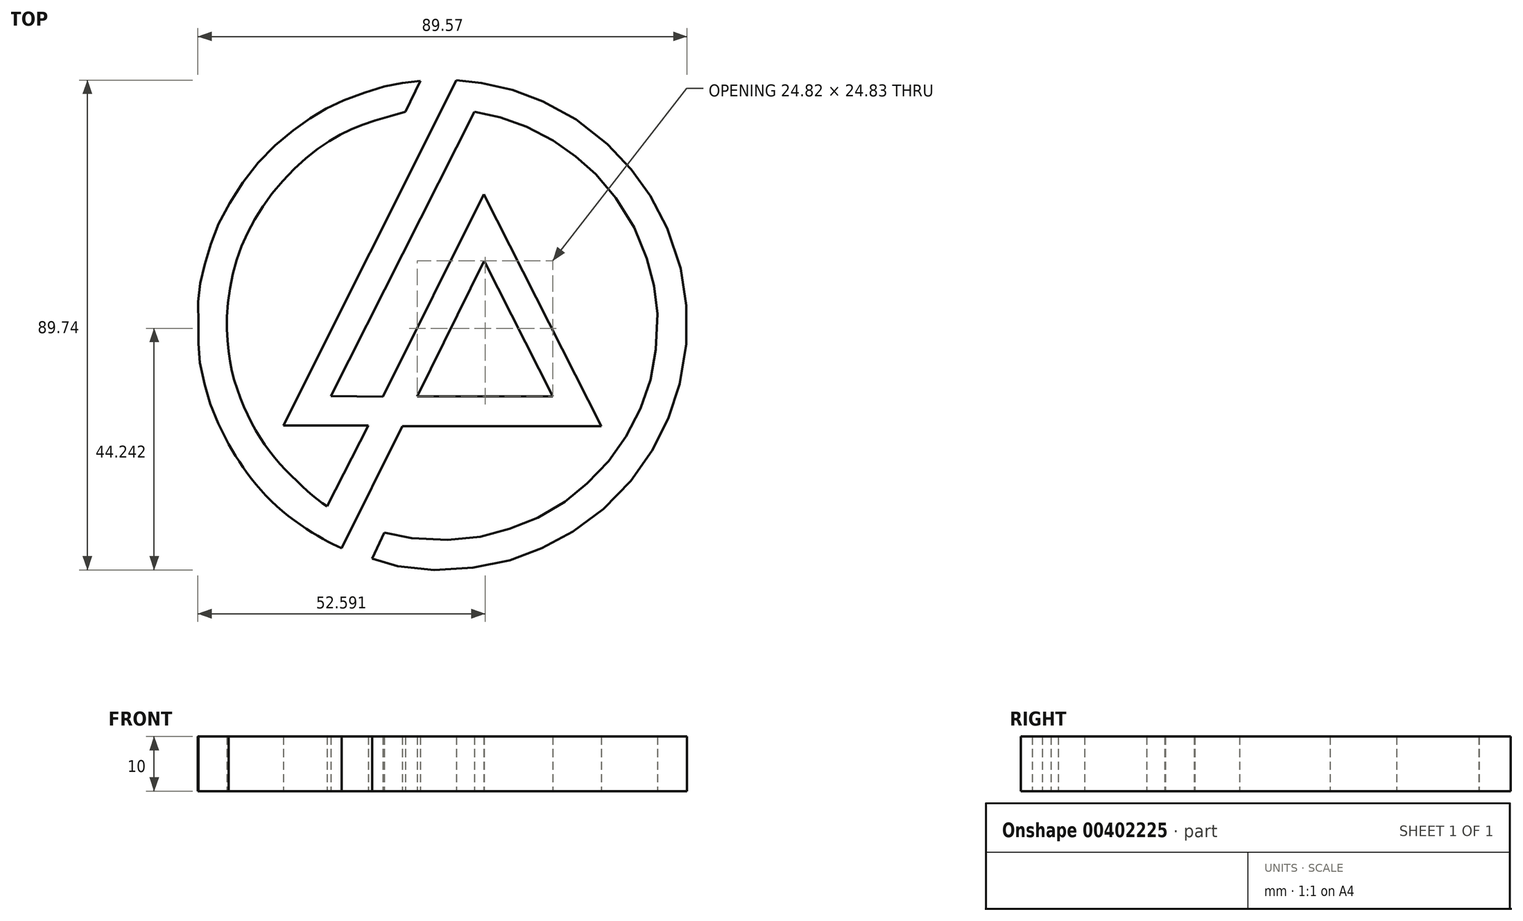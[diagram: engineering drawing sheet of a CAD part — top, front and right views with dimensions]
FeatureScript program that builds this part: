
annotation { "Feature Type Name" : "Feature", "Feature Type Description" : "" }
export const myFeature = defineFeature(function(context is Context, id is Id, definition is map)
    precondition{}
    {
        {
            var Q0;
            Q0=qCreatedBy(makeId("Top.planeOp"),FACE);
            var sketch = newSketch(context, id + "F0", { "sketchPlane" : qUnion([Q0])});
            skLineSegment(sketch, "E0", {"start": v(57.59, 61.86) * mm, "end": v(70.16, 37.03) * mm});
            skLineSegment(sketch, "E1", {"start": v(70.16, 37.03) * mm, "end": v(45.34, 37.03) * mm});
            skLineSegment(sketch, "E2", {"start": v(45.34, 37.03) * mm, "end": v(57.59, 61.86) * mm});
            skLineSegment(sketch, "E3", {"start": v(42.63, 31.52) * mm, "end": v(79.04, 31.57) * mm});
            skLineSegment(sketch, "E4", {"start": v(79.04, 31.57) * mm, "end": v(57.5, 74.01) * mm});
            skLineSegment(sketch, "E5", {"start": v(57.5, 74.01) * mm, "end": v(39.03, 36.95) * mm});
            skLineSegment(sketch, "E6", {"start": v(39.03, 36.95) * mm, "end": v(29.54, 37.05) * mm});
            skLineSegment(sketch, "E7", {"start": v(29.54, 37.05) * mm, "end": v(55.8, 89.1) * mm});
            skPoint(sketch, "E8.20.internal.snap0", {"position": v(57.75, 37.03) * mm});
            skFitSpline(sketch, "E8", {"points": [v(55.8, 89.1) * mm, v(59.81, 88.28) * mm, v(64.22, 86.85) * mm, v(69.09, 84.54) * mm, v(73.24, 81.82) * mm, v(76.4, 79.3) * mm, v(80, 75.56) * mm, v(83.94, 69.98) * mm, v(86.97, 63.6) * mm, v(88.43, 58.36) * mm, v(89.19, 54.41) * mm, v(89.15, 47.15) * mm, v(88.3, 41.07) * mm, v(86.67, 35.9) * mm, v(83.99, 30.4) * mm, v(80.96, 25.83) * mm, v(76.98, 21.55) * mm, v(73.24, 18.32) * mm, v(68.3, 15.22) * mm, v(63.05, 13.04) * mm, v(57.75, 11.44) * mm, v(51.51, 10.74) * mm, v(43.83, 11.09) * mm, v(39.29, 12.04) * mm], "startDerivative": vector(106.77, -19.5) * mm, "endDerivative": vector(-104.9, 26.78) * mm});
            skFitSpline(sketch, "E9", {"points": [v(39.29, 12.04) * mm, v(37.06, 7.3) * mm], "startDerivative": vector(-2.23, -4.74) * mm, "endDerivative": vector(-2.23, -4.74) * mm});
            skFitSpline(sketch, "E10", {"points": [v(37.06, 7.3) * mm, v(39.5, 6.44) * mm, v(45.19, 5.4) * mm, v(51.78, 5.28) * mm, v(59.25, 6.2) * mm, v(64.68, 7.77) * mm, v(70.05, 10.09) * mm, v(75.28, 13.17) * mm, v(80.86, 17.68) * mm, v(85.7, 23.06) * mm, v(89.05, 28.28) * mm, v(91.69, 33.92) * mm, v(93.65, 40.2) * mm, v(94.68, 47.98) * mm, v(94.5, 54.8) * mm, v(93.3, 61.6) * mm, v(90.28, 69.64) * mm, v(87.43, 74.63) * mm, v(84.41, 78.75) * mm, v(80.47, 82.94) * mm, v(74.58, 87.6) * mm, v(68.54, 90.93) * mm, v(63.88, 92.77) * mm, v(59.31, 94) * mm, v(54.8, 94.77) * mm, v(52.53, 94.94) * mm], "startDerivative": vector(81.47, -32.98) * mm, "endDerivative": vector(-83.27, 4.17) * mm});
            skLineSegment(sketch, "E11", {"start": v(52.53, 94.94) * mm, "end": v(20.85, 31.68) * mm});
            skLineSegment(sketch, "E12", {"start": v(20.85, 31.68) * mm, "end": v(36.37, 31.68) * mm});
            skLineSegment(sketch, "E13", {"start": v(36.37, 31.68) * mm, "end": v(28.84, 16.85) * mm});
            skFitSpline(sketch, "E14", {"points": [v(28.84, 16.85) * mm, v(24.72, 20.15) * mm, v(19.07, 25.94) * mm, v(14.13, 33.91) * mm, v(10.8, 45.27) * mm], "startDerivative": vector(-21.9, 12.86) * mm, "endDerivative": vector(-4.19, 41.47) * mm});
            skFitSpline(sketch, "E15", {"points": [v(10.8, 45.27) * mm, v(10.49, 49.3) * mm, v(10.8, 55.3) * mm, v(12.36, 62.26) * mm, v(15.25, 68.9) * mm, v(19.98, 75.67) * mm, v(26.19, 81.63) * mm, v(31.34, 84.98) * mm, v(35.75, 86.92) * mm, v(43.16, 89.11) * mm], "startDerivative": vector(-4.94, 44.07) * mm, "endDerivative": vector(66.09, 18.06) * mm});
            skFitSpline(sketch, "E16", {"points": [v(43.16, 89.11) * mm, v(45.91, 94.8) * mm], "startDerivative": vector(2.75, 5.68) * mm, "endDerivative": vector(2.75, 5.68) * mm});
            skFitSpline(sketch, "E17", {"points": [v(45.91, 94.8) * mm, v(41.82, 94.3) * mm, v(37.41, 93.2) * mm, v(31.7, 91.16) * mm, v(27.6, 89.11) * mm, v(23.54, 86.43) * mm, v(18.32, 82.05) * mm, v(13.41, 76.23) * mm, v(9.6, 69.91) * mm, v(7.34, 64.4) * mm, v(5.9, 59) * mm, v(5.2, 54.99) * mm, v(5.3, 48.85) * mm, v(5.3, 44.79) * mm, v(6.46, 38.93) * mm, v(7.98, 34.1) * mm, v(10.8, 28.24) * mm], "startDerivative": vector(-76.04, -7.22) * mm, "endDerivative": vector(47.77, -84.01) * mm});
            skFitSpline(sketch, "E18", {"points": [v(10.8, 28.24) * mm, v(14.89, 21.98) * mm, v(21, 15.69) * mm, v(27.47, 11.24) * mm, v(31.5, 9.16) * mm], "startDerivative": vector(14.59, -24.52) * mm, "endDerivative": vector(19.04, -9.16) * mm});
            skLineSegment(sketch, "E19", {"start": v(31.5, 9.16) * mm, "end": v(42.63, 31.52) * mm});
            skSolve(sketch);
        }
        {
            var Q0;
            Q0 = qSketchRegion(id + "F0", true);
            extrude(context, id + "F1", {"entities" : qUnion([Q0]), "depth" : 10 * mm, "offsetDistance" : 25 * mm});
        }
    });
